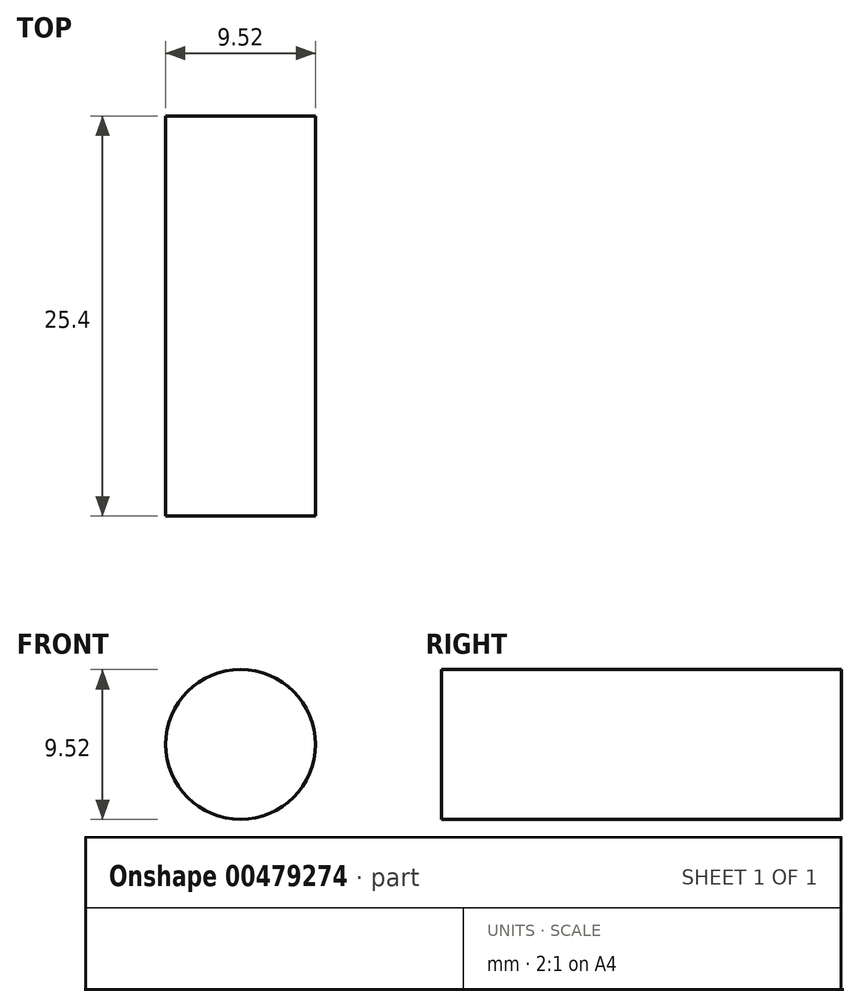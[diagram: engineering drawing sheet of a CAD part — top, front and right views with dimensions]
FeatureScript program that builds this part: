
annotation { "Feature Type Name" : "Feature", "Feature Type Description" : "" }
export const myFeature = defineFeature(function(context is Context, id is Id, definition is map)
    precondition{}
    {
        {
            var Q0;
            Q0=qCreatedBy(makeId("Front.planeOp"),FACE);
            var sketch = newSketch(context, id + "F0", { "sketchPlane" : qUnion([Q0])});
            skCircle(sketch, "E0", {"center": v(-20.82, 18.34) * mm, "radius": 4.76 * mm});
            skSolve(sketch);
        }
        {
            var Q0;
            Q0=makeQuery(id+"F0.imprint","IMPRINT",FACE,{"disambiguationData":[TD([[makeQuery(id+"F0.imprint","IMPRINT",EDGE,{"derivedFrom":sQuery(id+"F0.wireOp",EDGE,"E0")}),1.0]])]});
            extrude(context, id + "F1", {"entities" : qUnion([Q0]), "depth" : 25.4 * mm});
        }
    });
